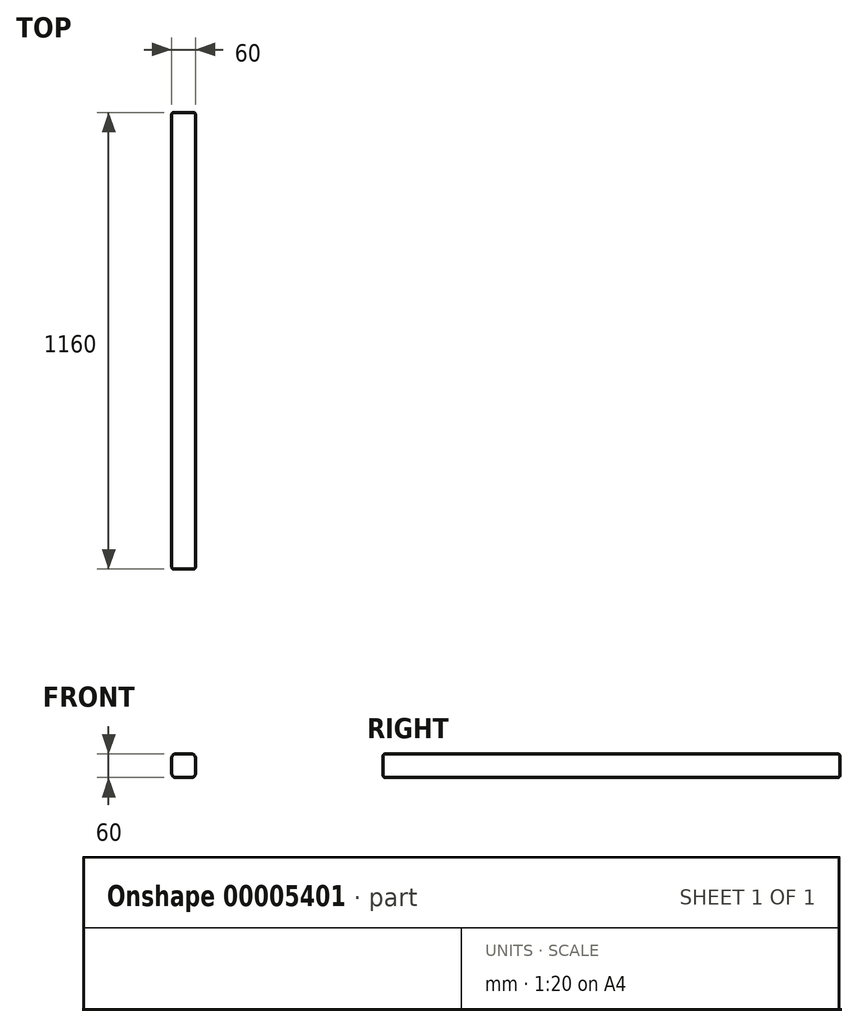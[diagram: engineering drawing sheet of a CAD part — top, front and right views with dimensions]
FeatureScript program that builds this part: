
annotation { "Feature Type Name" : "Feature", "Feature Type Description" : "" }
export const myFeature = defineFeature(function(context is Context, id is Id, definition is map)
    precondition{}
    {
        {
            var Q0;
            Q0=qCreatedBy(makeId("Front.planeOp"),FACE);
            var sketch = newSketch(context, id + "F0", { "sketchPlane" : qUnion([Q0])});
            skLineSegment(sketch, "E0.bottom", {"start": v(-51.64, 48.94) * mm, "end": v(-11.64, 48.94) * mm});
            skLineSegment(sketch, "E0.top", {"start": v(-51.64, -11.06) * mm, "end": v(-11.64, -11.06) * mm});
            skLineSegment(sketch, "E0.left", {"start": v(-61.64, 38.94) * mm, "end": v(-61.64, -1.06) * mm});
            skLineSegment(sketch, "E0.right", {"start": v(-1.64, 38.94) * mm, "end": v(-1.64, -1.06) * mm});
            skLineSegment(sketch, "E1.0", {"start": v(-51.64, 43.94) * mm, "end": v(-11.64, 43.94) * mm});
            skLineSegment(sketch, "E2.0", {"start": v(-51.64, -6.06) * mm, "end": v(-11.64, -6.06) * mm});
            skLineSegment(sketch, "E2.1", {"start": v(-56.64, 38.94) * mm, "end": v(-56.64, -1.06) * mm});
            skLineSegment(sketch, "E3.0", {"start": v(-6.64, 38.94) * mm, "end": v(-6.64, -1.06) * mm});
            skPoint(sketch, "E4.visualSharp", {"position": v(-61.64, 48.94) * mm});
            skArc(sketch, "E4.filletArc", {"start": v(-51.64, 48.94) * mm, "mid": v(-58.7, 46) * mm, "end": v(-61.64, 38.94) * mm});
            skPoint(sketch, "E5.visualSharp", {"position": v(-1.64, 48.94) * mm});
            skArc(sketch, "E5.filletArc", {"start": v(-1.64, 38.94) * mm, "mid": v(-4.57, 46) * mm, "end": v(-11.64, 48.94) * mm});
            skPoint(sketch, "E6.visualSharp", {"position": v(-1.64, -11.06) * mm});
            skArc(sketch, "E6.filletArc", {"start": v(-11.64, -11.06) * mm, "mid": v(-4.57, -8.14) * mm, "end": v(-1.64, -1.06) * mm});
            skPoint(sketch, "E7.visualSharp", {"position": v(-61.64, -11.06) * mm});
            skArc(sketch, "E7.filletArc", {"start": v(-61.64, -1.06) * mm, "mid": v(-58.7, -8.14) * mm, "end": v(-51.64, -11.06) * mm});
            skPoint(sketch, "E8.visualSharp", {"position": v(-56.64, 43.94) * mm});
            skArc(sketch, "E8.filletArc", {"start": v(-51.64, 43.94) * mm, "mid": v(-55.17, 42.47) * mm, "end": v(-56.64, 38.94) * mm});
            skPoint(sketch, "E9.visualSharp", {"position": v(-56.64, -6.06) * mm});
            skArc(sketch, "E9.filletArc", {"start": v(-56.64, -1.06) * mm, "mid": v(-55.17, -4.6) * mm, "end": v(-51.64, -6.06) * mm});
            skPoint(sketch, "E10.visualSharp", {"position": v(-6.64, -6.06) * mm});
            skArc(sketch, "E10.filletArc", {"start": v(-11.64, -6.06) * mm, "mid": v(-8.1, -4.6) * mm, "end": v(-6.64, -1.06) * mm});
            skPoint(sketch, "E11.visualSharp", {"position": v(-6.64, 43.94) * mm});
            skArc(sketch, "E11.filletArc", {"start": v(-6.64, 38.94) * mm, "mid": v(-8.1, 42.47) * mm, "end": v(-11.64, 43.94) * mm});
            skSolve(sketch);
        }
        {
            var Q0;
            Q0=makeQuery(id+"F0.imprint","IMPRINT",FACE,{"disambiguationData":[TD([[makeQuery(id+"F0.imprint","IMPRINT",EDGE,{"derivedFrom":sQuery(id+"F0.wireOp",EDGE,"E1.0")}),-1.0]])]});
            var Q1;
            Q1=makeQuery(id+"F0.imprint","IMPRINT",FACE,{"disambiguationData":[TD([[makeQuery(id+"F0.imprint","IMPRINT",EDGE,{"derivedFrom":sQuery(id+"F0.wireOp",EDGE,"E0.bottom")}),-1.0]])]});
            extrude(context, id + "F1", {"entities" : qUnion([Q0, Q1]), "depth" : 1160 * mm});
        }
        {
            var Q0;
            Q0=makeQuery(id+"F1.opExtrude","CAP_EDGE",EDGE,{"disambiguationData":[OSD([sQuery(id+"F0.wireOp",EDGE,"E0.left")])],"isStart":true});
            var Q1;
            Q1=makeQuery(id+"F1.opExtrude","CAP_EDGE",EDGE,{"disambiguationData":[OSD([sQuery(id+"F0.wireOp",EDGE,"E0.left")])],"isStart":false});
            fillet(context, id + "F2", {"entities" : qUnion([Q0, Q1]), "radius" : 5 * mm, "tangentPropagation" : true, "allowEdgeOverflow" : false});
        }
    });
